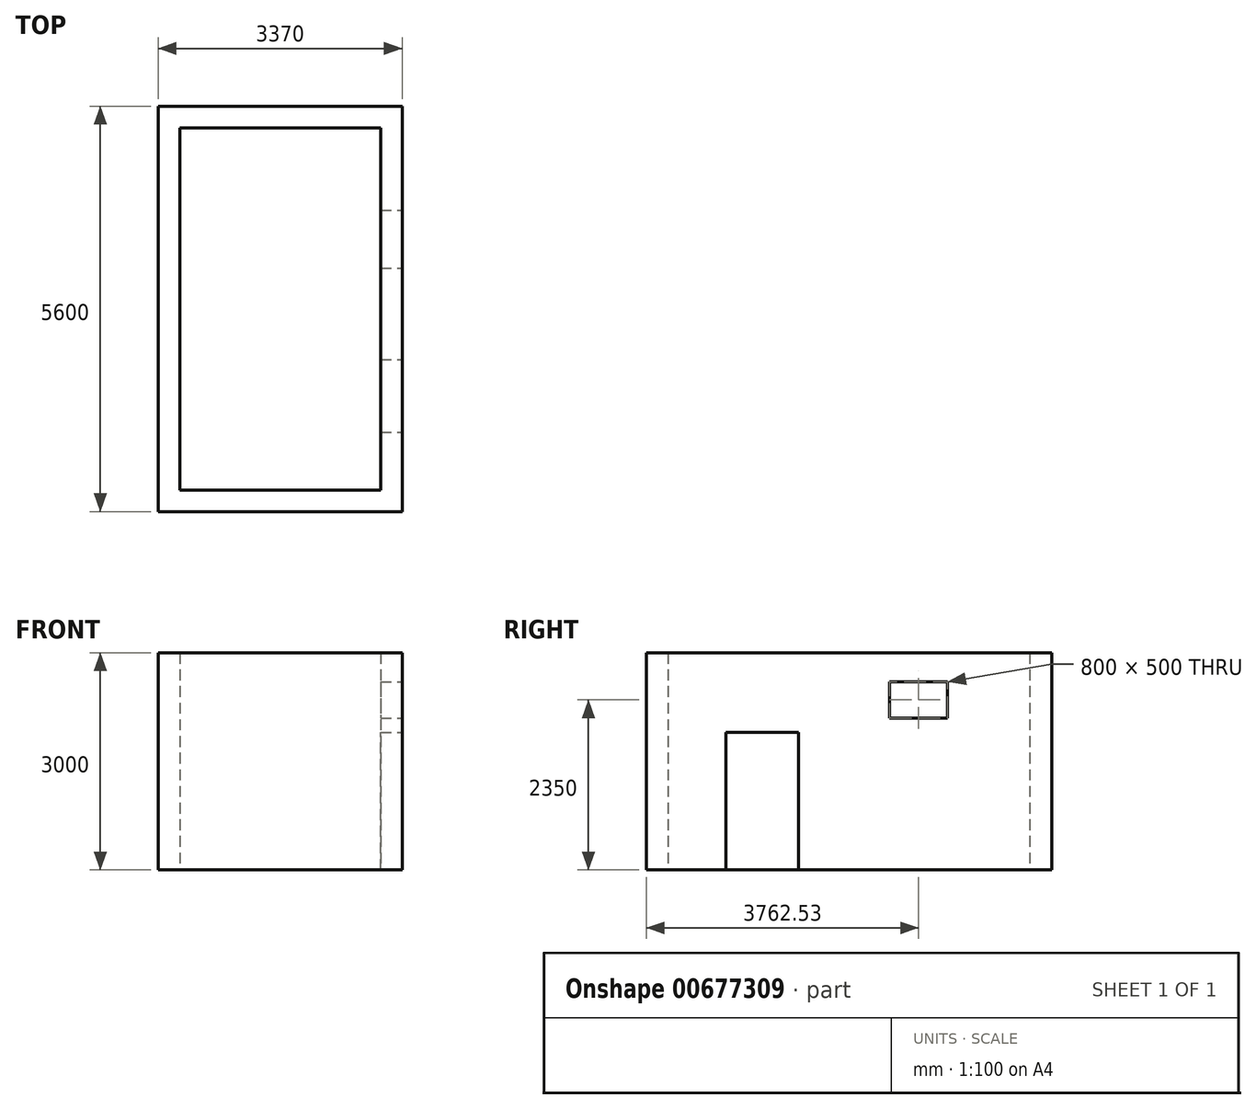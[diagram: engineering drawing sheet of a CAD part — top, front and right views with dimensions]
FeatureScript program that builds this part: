
annotation { "Feature Type Name" : "Feature", "Feature Type Description" : "" }
export const myFeature = defineFeature(function(context is Context, id is Id, definition is map)
    precondition{}
    {
        {
            var Q0;
            Q0=qCreatedBy(makeId("Top.planeOp"),FACE);
            var sketch = newSketch(context, id + "F0", { "sketchPlane" : qUnion([Q0])});
            skLineSegment(sketch, "E0.bottom", {"start": v(0, 0) * mm, "end": v(2770, 0) * mm});
            skLineSegment(sketch, "E0.top", {"start": v(0, 5000) * mm, "end": v(2770, 5000) * mm});
            skLineSegment(sketch, "E0.left", {"start": v(0, 0) * mm, "end": v(0, 5000) * mm});
            skLineSegment(sketch, "E0.right", {"start": v(2770, 0) * mm, "end": v(2770, 5000) * mm});
            skLineSegment(sketch, "E1.bottom", {"start": v(-300, -300) * mm, "end": v(3070, -300) * mm});
            skLineSegment(sketch, "E1.top", {"start": v(-300, 5300) * mm, "end": v(3070, 5300) * mm});
            skLineSegment(sketch, "E1.left", {"start": v(-300, -300) * mm, "end": v(-300, 5300) * mm});
            skLineSegment(sketch, "E1.right", {"start": v(3070, -300) * mm, "end": v(3070, 5300) * mm});
            skLineSegment(sketch, "E2.bottom", {"start": v(2770, 5000) * mm, "end": v(2470, 5000) * mm});
            skLineSegment(sketch, "E2.top", {"start": v(2770, 4600) * mm, "end": v(2470, 4600) * mm});
            skLineSegment(sketch, "E2.left", {"start": v(2770, 5000) * mm, "end": v(2770, 4600) * mm});
            skLineSegment(sketch, "E2.right", {"start": v(2470, 5000) * mm, "end": v(2470, 4600) * mm});
            skSolve(sketch);
        }
        {
            var Q0;
            Q0 = qSketchRegion(id + "F0", true);
            var Q1;
            Q1=makeQuery(id+"F0.imprint","IMPRINT",FACE,{"disambiguationData":[TD([[makeQuery(id+"F0.imprint","IMPRINT",EDGE,{"derivedFrom":sQuery(id+"F0.wireOp",EDGE,"E2.bottom")}),1.0]])]});
            extrude(context, id + "F1", {"entities" : qUnion([Q0, Q1]), "depth" : 3000 * mm, "offsetDistance" : 25 * mm});
        }
        {
            var Q0;
            Q0=makeQuery(id+"F1.opExtrude","SWEPT_FACE",FACE,{"disambiguationData":[OSD([sQuery(id+"F0.wireOp",EDGE,"E1.right")])]});
            var sketch = newSketch(context, id + "F2", { "sketchPlane" : qUnion([Q0])});
            skLineSegment(sketch, "E3.bottom", {"start": v(800, 0) * mm, "end": v(1800, 0) * mm});
            skLineSegment(sketch, "E3.top", {"start": v(800, 1900) * mm, "end": v(1800, 1900) * mm});
            skLineSegment(sketch, "E3.left", {"start": v(800, 0) * mm, "end": v(800, 1900) * mm});
            skLineSegment(sketch, "E3.right", {"start": v(1800, 0) * mm, "end": v(1800, 1900) * mm});
            skLineSegment(sketch, "E4.bottom", {"start": v(3062.53, 2600) * mm, "end": v(3862.53, 2600) * mm});
            skLineSegment(sketch, "E4.top", {"start": v(3062.53, 2100) * mm, "end": v(3862.53, 2100) * mm});
            skLineSegment(sketch, "E4.left", {"start": v(3062.53, 2600) * mm, "end": v(3062.53, 2100) * mm});
            skLineSegment(sketch, "E4.right", {"start": v(3862.53, 2600) * mm, "end": v(3862.53, 2100) * mm});
            skSolve(sketch);
        }
        {
            var Q0;
            Q0 = qSketchRegion(id + "F2", true);
            extrude(context, id + "F3", {"entities" : qUnion([Q0]), "operationType" : NewBodyOperationType.REMOVE, "endBound" : BoundingType.UP_TO_NEXT, "oppositeDirection" : true, "depth" : 25 * mm, "offsetDistance" : 25 * mm});
        }
    });
